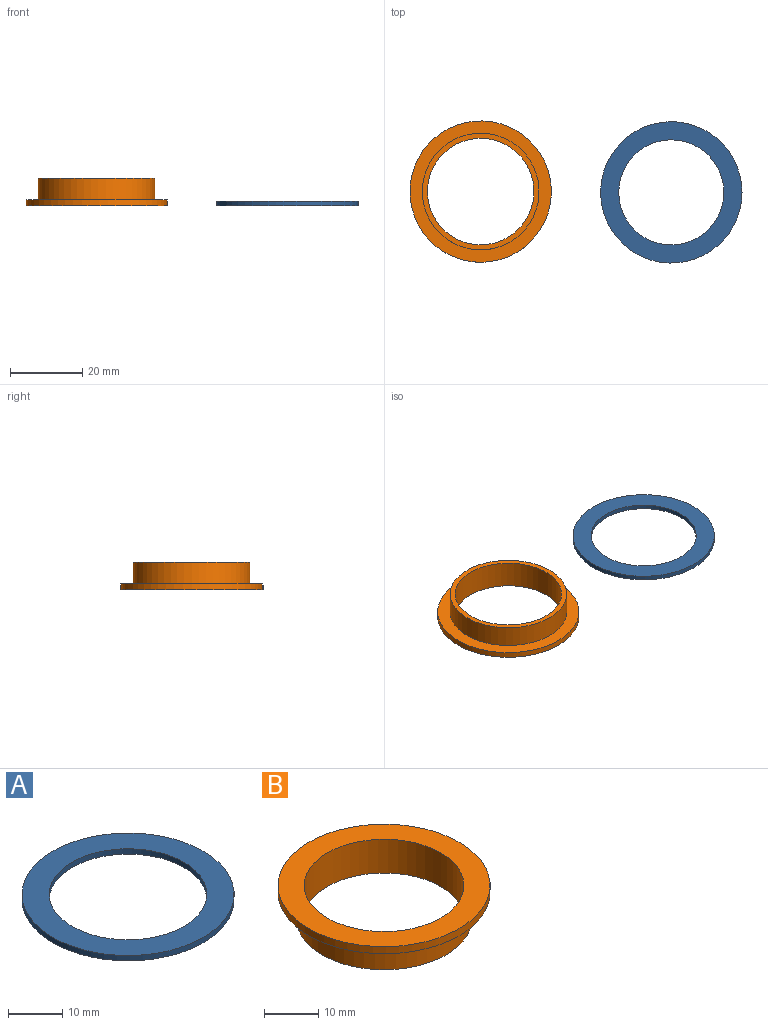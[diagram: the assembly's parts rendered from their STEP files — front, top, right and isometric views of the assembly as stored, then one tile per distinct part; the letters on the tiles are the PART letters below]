
ASSEMBLY  parts=2 mates=1
PART A: 4 faces, bbox 39x39x1.2 mm
  f0: cylinder r=14.5mm len=29mm, axis (0,0,-1), area 109.3mm2, adj f2,f3
  f1: cylinder r=19.5mm len=39mm, axis (0,0,-1), area 147mm2, adj f2,f3
  f2: plane 39x39mm, normal (0,0,1), area 534.1mm2, adj f0,f1
  f3: plane 39x39mm, normal (0,0,-1), area 534.1mm2, adj f0,f1
PART B: 6 faces, bbox 39x39x7.6 mm
  f0: cylinder r=14.7mm len=29.4mm, axis (0,0,-1), area 702mm2, adj f2,f5
  f1: cylinder r=19.5mm len=39mm, axis (0,0,-1), area 196mm2, adj f2,f3
  f2: plane 39x39mm, normal (0,0,1), area 515.7mm2, adj f0,f1
  f3: plane 39x39mm, normal (0,0,-1), area 380.3mm2, adj f1,f4
  f4: cylinder r=16.1mm len=32.2mm, axis (0,0,1), area 607mm2, adj f3,f5
  f5: plane 32.2x32.2mm, normal (0,0,-1), area 135.5mm2, adj f0,f4
PLACE A t=(27.37,-1.08,-25.11)mm
PLACE B rot(axis=(0,1,0),180deg) t=(-25.23,-0.86,-23.51)mm
MATE planar B.f1 <-> A.f1  axis (0,0,-1) through (-25.23,-0.86,-0.11)mm
